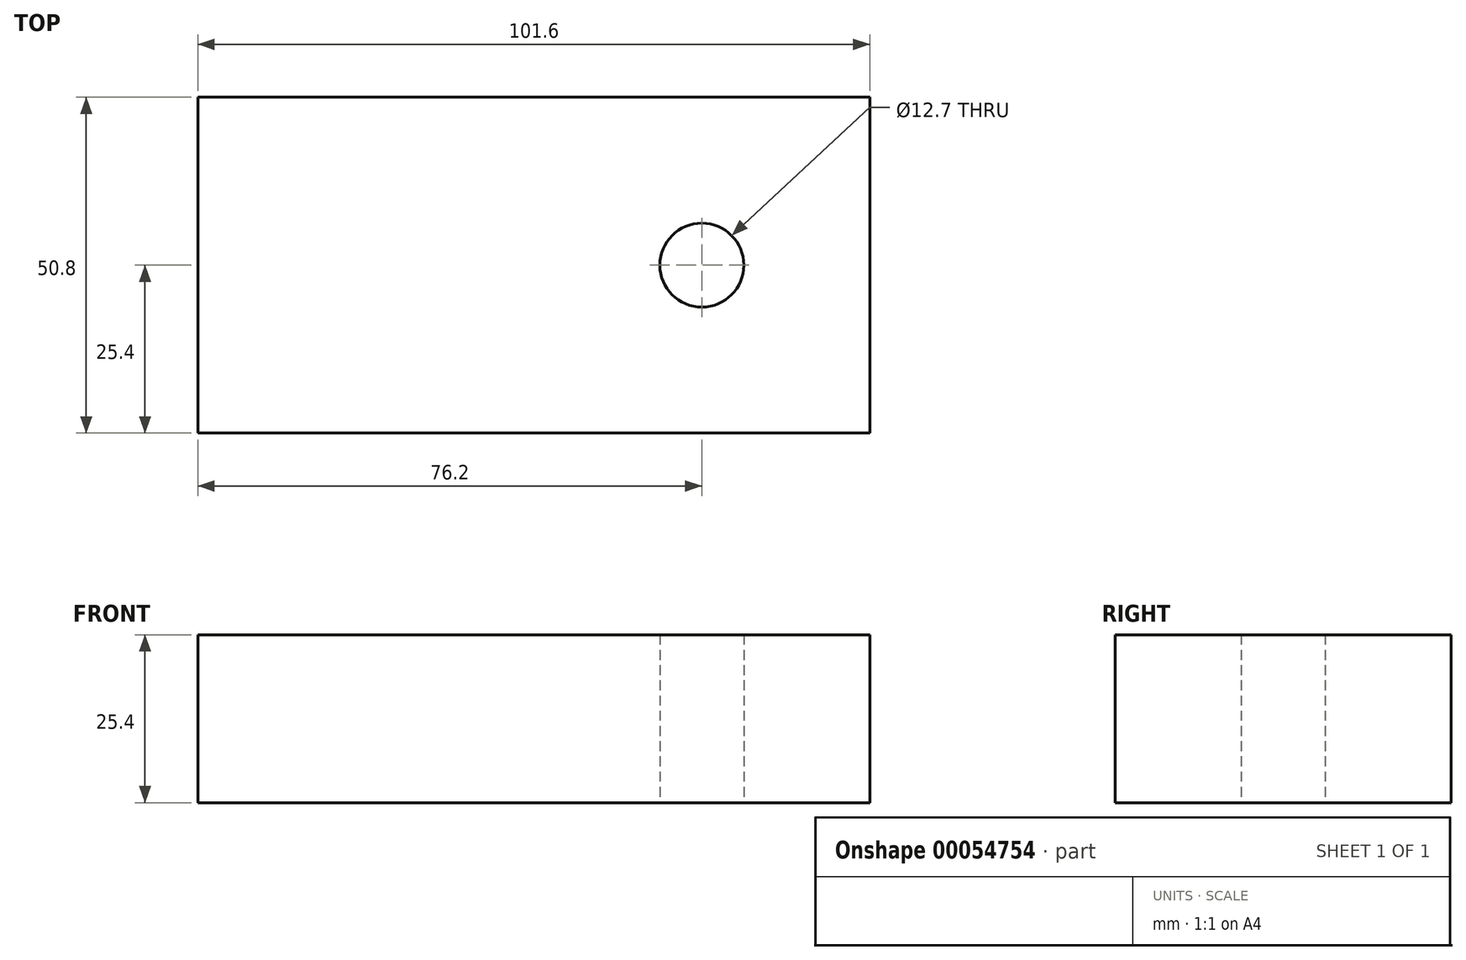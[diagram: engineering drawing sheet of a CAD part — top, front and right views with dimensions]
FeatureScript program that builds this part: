
annotation { "Feature Type Name" : "Feature", "Feature Type Description" : "" }
export const myFeature = defineFeature(function(context is Context, id is Id, definition is map)
    precondition{}
    {
        {
            var Q0;
            Q0=qCreatedBy(makeId("Top.planeOp"),FACE);
            cPlane(context, id + "F0", {"entities" : qUnion([Q0]), "cplaneType" : CPlaneType.OFFSET, "offset" : 152.4 * mm, "width" : 152.4 * mm, "height" : 152.4 * mm});
        }
        {
            var Q0;
            Q0=qCreatedBy(id+"F0.planeOp",FACE);
            var sketch = newSketch(context, id + "F1", { "sketchPlane" : qUnion([Q0])});
            skLineSegment(sketch, "E0.bottom", {"start": v(-50.8, 25.4) * mm, "end": v(50.8, 25.4) * mm});
            skLineSegment(sketch, "E0.top", {"start": v(-50.8, -25.4) * mm, "end": v(50.8, -25.4) * mm});
            skLineSegment(sketch, "E0.left", {"start": v(-50.8, 25.4) * mm, "end": v(-50.8, -25.4) * mm});
            skLineSegment(sketch, "E0.right", {"start": v(50.8, 25.4) * mm, "end": v(50.8, -25.4) * mm});
            skCircle(sketch, "E1", {"center": v(25.4, 0) * mm, "radius": 6.35 * mm});
            skSolve(sketch);
        }
        {
            var Q0;
            Q0=makeQuery(id+"F1.imprint","IMPRINT",FACE,{"disambiguationData":[TD([[makeQuery(id+"F1.imprint","IMPRINT",EDGE,{"derivedFrom":sQuery(id+"F1.wireOp",EDGE,"E0.bottom")}),-1.0]])]});
            extrude(context, id + "F2", {"entities" : qUnion([Q0]), "depth" : 25.4 * mm});
        }
    });
